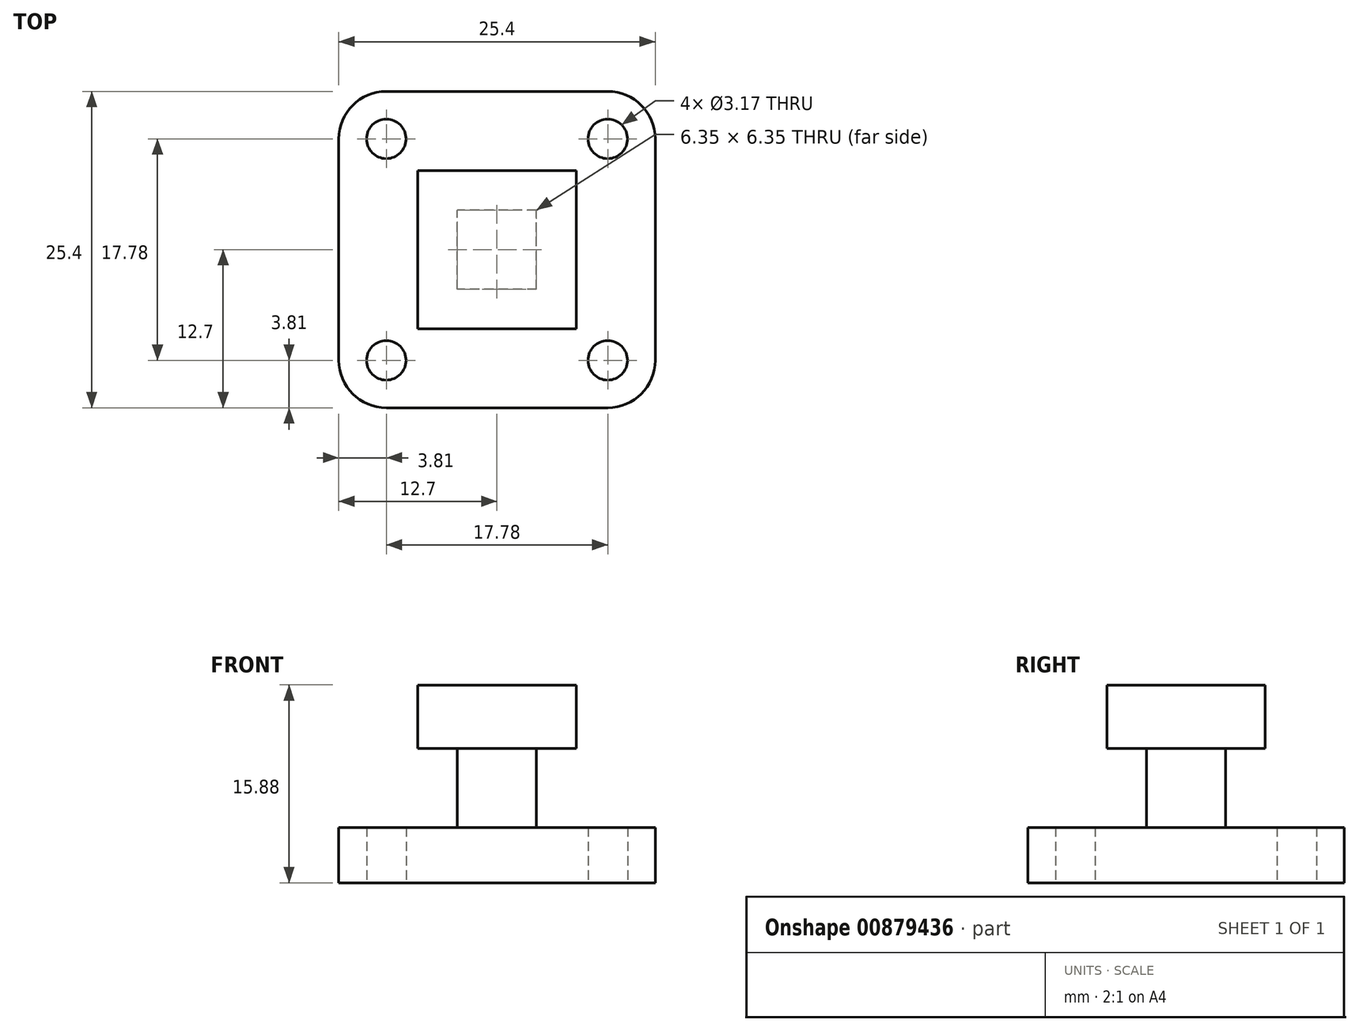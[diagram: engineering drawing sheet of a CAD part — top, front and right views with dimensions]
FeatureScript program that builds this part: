
annotation { "Feature Type Name" : "Feature", "Feature Type Description" : "" }
export const myFeature = defineFeature(function(context is Context, id is Id, definition is map)
    precondition{}
    {
        {
            var Q0;
            Q0=qCreatedBy(makeId("Top.planeOp"),FACE);
            var sketch = newSketch(context, id + "F0", { "sketchPlane" : qUnion([Q0])});
            skLineSegment(sketch, "E0.bottom", {"start": v(8.9, 12.7) * mm, "end": v(-8.9, 12.7) * mm});
            skLineSegment(sketch, "E0.top", {"start": v(8.9, -12.7) * mm, "end": v(-8.9, -12.7) * mm});
            skLineSegment(sketch, "E0.left", {"start": v(12.7, 8.9) * mm, "end": v(12.7, -8.9) * mm});
            skLineSegment(sketch, "E0.right", {"start": v(-12.7, 8.9) * mm, "end": v(-12.7, -8.9) * mm});
            skPoint(sketch, "E0.middle", {"position": v(0, 0) * mm});
            skCircle(sketch, "E1", {"center": v(-8.9, 8.9) * mm, "radius": 1.59 * mm});
            skPoint(sketch, "E2.visualSharp", {"position": v(-12.7, 12.7) * mm});
            skArc(sketch, "E2.filletArc", {"start": v(-8.9, 12.7) * mm, "mid": v(-11.58, 11.58) * mm, "end": v(-12.7, 8.9) * mm});
            skArc(sketch, "E3.MirrorCS", {"start": v(8.9, 12.7) * mm, "mid": v(11.58, 11.58) * mm, "end": v(12.7, 8.9) * mm});
            skCircle(sketch, "E4.MirrorC", {"center": v(8.9, 8.9) * mm, "radius": 1.59 * mm});
            skPoint(sketch, "E5.orphan", {"position": v(12.7, 12.7) * mm});
            skArc(sketch, "E6.MirrorCS", {"start": v(-8.9, -12.7) * mm, "mid": v(-11.58, -11.58) * mm, "end": v(-12.7, -8.9) * mm});
            skCircle(sketch, "E7.MirrorC", {"center": v(-8.9, -8.9) * mm, "radius": 1.59 * mm});
            skCircle(sketch, "E8.MirrorC", {"center": v(8.9, -8.9) * mm, "radius": 1.59 * mm});
            skArc(sketch, "E9.MirrorCS", {"start": v(8.9, -12.7) * mm, "mid": v(11.58, -11.58) * mm, "end": v(12.7, -8.9) * mm});
            skPoint(sketch, "E10.orphan", {"position": v(12.7, -12.7) * mm});
            skPoint(sketch, "E11.orphan", {"position": v(-12.7, -12.7) * mm});
            skSolve(sketch);
        }
        {
            var Q0;
            Q0 = qSketchRegion(id + "F0", true);
            extrude(context, id + "F1", {"entities" : qUnion([Q0]), "depth" : 4.44 * mm, "offsetDistance" : 25.4 * mm});
        }
        {
            var Q0;
            Q0=makeQuery(id+"F1.opExtrude","CAP_FACE",FACE,{"disambiguationData":[OSD([sQuery(id+"F0.wireOp",EDGE,"E0.bottom"),sQuery(id+"F0.wireOp",EDGE,"E0.top"),sQuery(id+"F0.wireOp",EDGE,"E0.left"),sQuery(id+"F0.wireOp",EDGE,"E0.right"),sQuery(id+"F0.wireOp",EDGE,"E1"),sQuery(id+"F0.wireOp",EDGE,"E2.filletArc"),sQuery(id+"F0.wireOp",EDGE,"E3.MirrorCS"),sQuery(id+"F0.wireOp",EDGE,"E4.MirrorC"),sQuery(id+"F0.wireOp",EDGE,"E6.MirrorCS"),sQuery(id+"F0.wireOp",EDGE,"E7.MirrorC"),sQuery(id+"F0.wireOp",EDGE,"E8.MirrorC"),sQuery(id+"F0.wireOp",EDGE,"E9.MirrorCS")])],"isStart":false});
            var sketch = newSketch(context, id + "F2", { "sketchPlane" : qUnion([Q0])});
            skLineSegment(sketch, "E12.bottom", {"start": v(3.17, -3.17) * mm, "end": v(-3.18, -3.17) * mm});
            skLineSegment(sketch, "E12.top", {"start": v(3.17, 3.18) * mm, "end": v(-3.18, 3.18) * mm});
            skLineSegment(sketch, "E12.left", {"start": v(3.17, -3.17) * mm, "end": v(3.17, 3.18) * mm});
            skLineSegment(sketch, "E12.right", {"start": v(-3.18, -3.17) * mm, "end": v(-3.18, 3.18) * mm});
            skPoint(sketch, "E12.middle", {"position": v(0, 0) * mm});
            skSolve(sketch);
        }
        {
            var Q0;
            Q0 = qSketchRegion(id + "F2", true);
            extrude(context, id + "F3", {"entities" : qUnion([Q0]), "operationType" : NewBodyOperationType.ADD, "depth" : 6.35 * mm, "offsetDistance" : 25.4 * mm});
        }
        {
            var Q0;
            Q0=makeQuery(id+"F3.opExtrude","CAP_FACE",FACE,{"disambiguationData":[OSD([sQuery(id+"F2.wireOp",EDGE,"E12.bottom"),sQuery(id+"F2.wireOp",EDGE,"E12.top"),sQuery(id+"F2.wireOp",EDGE,"E12.left"),sQuery(id+"F2.wireOp",EDGE,"E12.right")])],"isStart":false});
            var sketch = newSketch(context, id + "F4", { "sketchPlane" : qUnion([Q0])});
            skLineSegment(sketch, "E13.bottom", {"start": v(6.35, -6.35) * mm, "end": v(-6.35, -6.35) * mm});
            skLineSegment(sketch, "E13.top", {"start": v(6.35, 6.35) * mm, "end": v(-6.35, 6.35) * mm});
            skLineSegment(sketch, "E13.left", {"start": v(6.35, -6.35) * mm, "end": v(6.35, 6.35) * mm});
            skLineSegment(sketch, "E13.right", {"start": v(-6.35, -6.35) * mm, "end": v(-6.35, 6.35) * mm});
            skPoint(sketch, "E13.middle", {"position": v(0, 0) * mm});
            skSolve(sketch);
        }
        {
            var Q0;
            Q0 = qSketchRegion(id + "F4", true);
            extrude(context, id + "F5", {"entities" : qUnion([Q0]), "operationType" : NewBodyOperationType.ADD, "depth" : 5.08 * mm, "offsetDistance" : 25.4 * mm});
        }
    });
